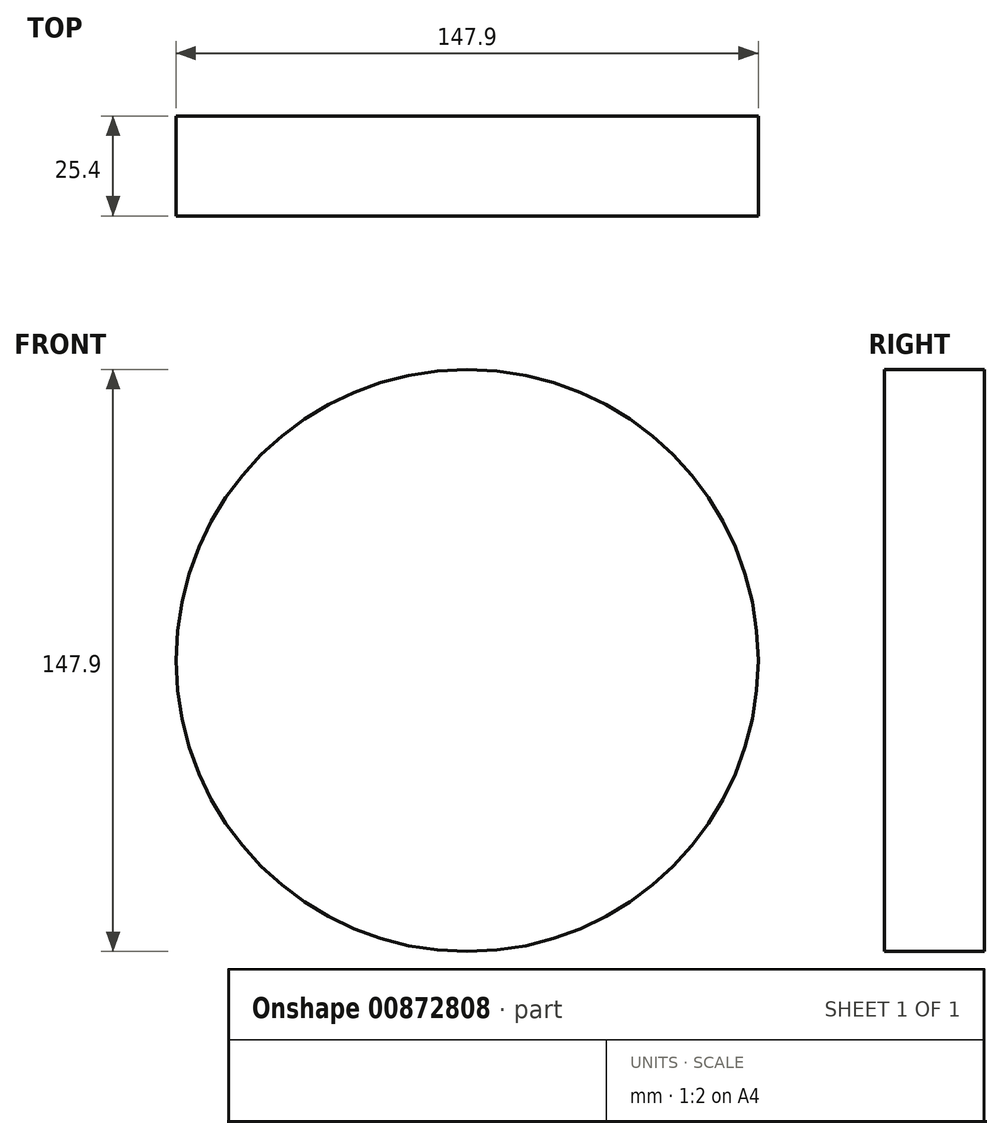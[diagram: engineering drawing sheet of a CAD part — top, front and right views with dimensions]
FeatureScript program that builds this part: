
annotation { "Feature Type Name" : "Feature", "Feature Type Description" : "" }
export const myFeature = defineFeature(function(context is Context, id is Id, definition is map)
    precondition{}
    {
        {
            var Q0;
            Q0=qCreatedBy(makeId("Front.planeOp"),FACE);
            var sketch = newSketch(context, id + "F0", { "sketchPlane" : qUnion([Q0])});
            skCircle(sketch, "E0", {"center": v(-9.05, 0) * mm, "radius": 73.95 * mm});
            skSolve(sketch);
        }
        {
            var Q0;
            Q0=qSketchRegion(id+"F0",true);
            extrude(context, id + "F1", {"entities" : qUnion([Q0]), "depth" : 25.4 * mm, "offsetDistance" : 25.4 * mm});
        }
    });
